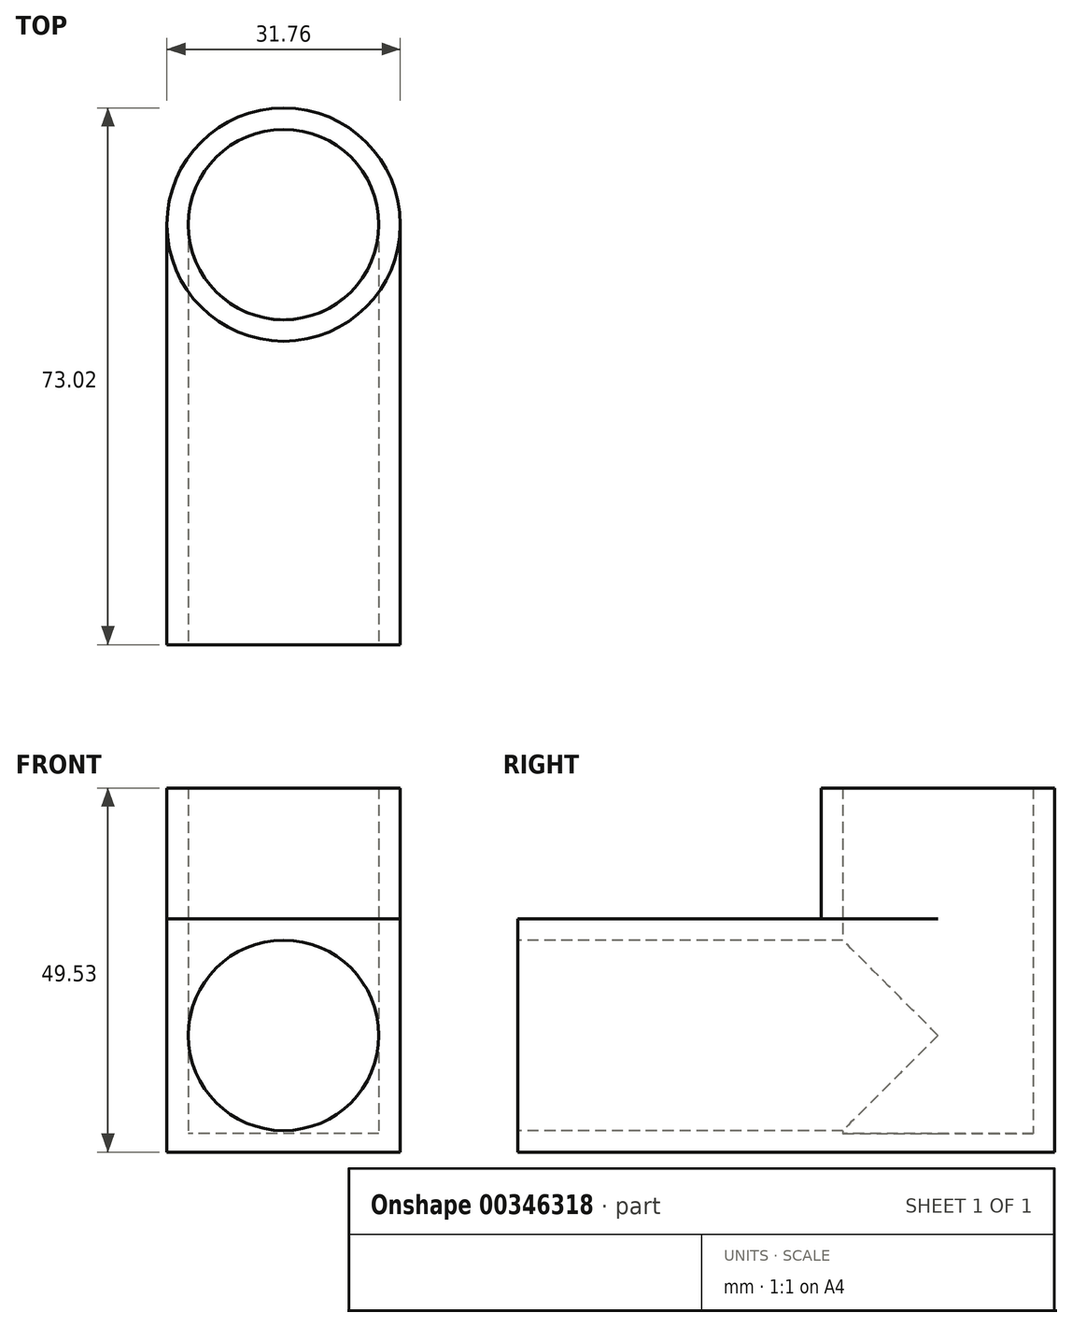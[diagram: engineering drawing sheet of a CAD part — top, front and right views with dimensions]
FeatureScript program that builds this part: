
annotation { "Feature Type Name" : "Feature", "Feature Type Description" : "" }
export const myFeature = defineFeature(function(context is Context, id is Id, definition is map)
    precondition{}
    {
        {
            var Q0;
            Q0=qCreatedBy(makeId("Top.planeOp"),FACE);
            var sketch = newSketch(context, id + "F0", { "sketchPlane" : qUnion([Q0])});
            skLineSegment(sketch, "E0.bottom", {"start": v(15.88, 36.51) * mm, "end": v(-15.87, 36.51) * mm});
            skLineSegment(sketch, "E0.top", {"start": v(15.88, -36.51) * mm, "end": v(-15.88, -36.51) * mm});
            skLineSegment(sketch, "E0.left", {"start": v(15.88, 36.51) * mm, "end": v(15.88, -36.51) * mm});
            skLineSegment(sketch, "E0.right", {"start": v(-15.87, 36.51) * mm, "end": v(-15.88, -36.51) * mm});
            skPoint(sketch, "E0.middle", {"position": v(0, 0) * mm});
            skSolve(sketch);
        }
        {
            var Q0;
            Q0=makeQuery(id+"F0.imprint","IMPRINT",FACE,{"disambiguationData":[TD([[makeQuery(id+"F0.imprint","IMPRINT",EDGE,{"derivedFrom":sQuery(id+"F0.wireOp",EDGE,"E0.bottom")}),1.0]])]});
            extrude(context, id + "F1", {"entities" : qUnion([Q0]), "depth" : 31.75 * mm});
        }
        {
            var Q0;
            Q0=makeQuery(id+"F1.opExtrude","CAP_FACE",FACE,{"disambiguationData":[OSD([sQuery(id+"F0.wireOp",EDGE,"E0.bottom"),sQuery(id+"F0.wireOp",EDGE,"E0.top"),sQuery(id+"F0.wireOp",EDGE,"E0.left"),sQuery(id+"F0.wireOp",EDGE,"E0.right")])],"isStart":false});
            var sketch = newSketch(context, id + "F2", { "sketchPlane" : qUnion([Q0])});
            skCircle(sketch, "E1", {"center": v(0, 20.64) * mm, "radius": 15.88 * mm});
            skCircle(sketch, "E2", {"center": v(0, 20.64) * mm, "radius": 12.95 * mm});
            skSolve(sketch);
        }
        {
            var Q0;
            Q0 = qSketchRegion(id + "F2", true);
            extrude(context, id + "F3", {"entities" : qUnion([Q0]), "operationType" : NewBodyOperationType.ADD, "depth" : 17.78 * mm});
        }
        {
            var Q0;
            {var subQ0=sQuery(id+"F0.wireOp",EDGE,"E0.bottom");var subQ1=sQuery(id+"F0.wireOp",EDGE,"E0.right");var subQ2=makeQuery(id+"F1.opExtrude","CAP_FACE",FACE,{"disambiguationData":[OSD([subQ0,sQuery(id+"F0.wireOp",EDGE,"E0.top"),sQuery(id+"F0.wireOp",EDGE,"E0.left"),subQ1])],"isStart":false});Q0=makeQuery(id+"F3.boolean.opBoolean","SPLIT",FACE,{"disambiguationData":[TD([makeQuery(id+"F1.opExtrude","SWEPT_FACE",FACE,{"disambiguationData":[OSD([subQ0])]}),subQ2,makeQuery(id+"F1.opExtrude","SWEPT_FACE",FACE,{"disambiguationData":[OSD([subQ1])]}),makeQuery(id+"F3.opExtrude","SWEPT_FACE",FACE,{"disambiguationData":[OSD([sQuery(id+"F2.wireOp",EDGE,"E1")])]})])],"derivedFrom":subQ2});}
            extrude(context, id + "F4", {"entities" : qUnion([Q0]), "operationType" : NewBodyOperationType.REMOVE, "endBound" : BoundingType.THROUGH_ALL, "oppositeDirection" : true, "depth" : 25.4 * mm});
        }
        {
            var Q0;
            {var subQ0=sQuery(id+"F0.wireOp",EDGE,"E0.bottom");var subQ1=sQuery(id+"F0.wireOp",EDGE,"E0.left");var subQ2=makeQuery(id+"F1.opExtrude","CAP_FACE",FACE,{"disambiguationData":[OSD([subQ0,sQuery(id+"F0.wireOp",EDGE,"E0.top"),subQ1,sQuery(id+"F0.wireOp",EDGE,"E0.right")])],"isStart":false});Q0=makeQuery(id+"F3.boolean.opBoolean","SPLIT",FACE,{"disambiguationData":[TD([makeQuery(id+"F1.opExtrude","SWEPT_FACE",FACE,{"disambiguationData":[OSD([subQ0])]}),subQ2,makeQuery(id+"F1.opExtrude","SWEPT_FACE",FACE,{"disambiguationData":[OSD([subQ1])]}),makeQuery(id+"F3.opExtrude","SWEPT_FACE",FACE,{"disambiguationData":[OSD([sQuery(id+"F2.wireOp",EDGE,"E1")])]})])],"derivedFrom":subQ2});}
            extrude(context, id + "F5", {"entities" : qUnion([Q0]), "operationType" : NewBodyOperationType.REMOVE, "endBound" : BoundingType.THROUGH_ALL, "oppositeDirection" : true, "depth" : 25.4 * mm});
        }
        {
            var Q0;
            Q0=makeQuery(id+"F3.boolean.opBoolean","SPLIT",FACE,{"disambiguationData":[TD([makeQuery(id+"F3.opExtrude","SWEPT_FACE",FACE,{"disambiguationData":[OSD([sQuery(id+"F2.wireOp",EDGE,"E2")])]})])],"derivedFrom":makeQuery(id+"F1.opExtrude","CAP_FACE",FACE,{"disambiguationData":[OSD([sQuery(id+"F0.wireOp",EDGE,"E0.bottom"),sQuery(id+"F0.wireOp",EDGE,"E0.top"),sQuery(id+"F0.wireOp",EDGE,"E0.left"),sQuery(id+"F0.wireOp",EDGE,"E0.right")])],"isStart":false})});
            extrude(context, id + "F6", {"entities" : qUnion([Q0]), "operationType" : NewBodyOperationType.REMOVE, "oppositeDirection" : true, "depth" : 29.2 * mm});
        }
        {
            var Q0;
            Q0=makeQuery(id+"F1.opExtrude","SWEPT_FACE",FACE,{"disambiguationData":[OSD([sQuery(id+"F0.wireOp",EDGE,"E0.top")])]});
            var sketch = newSketch(context, id + "F7", { "sketchPlane" : qUnion([Q0])});
            skCircle(sketch, "E3", {"center": v(0, 15.88) * mm, "radius": 12.95 * mm});
            skPoint(sketch, "E3.centerSnap0", {"position": v(-15.88, 15.88) * mm});
            skSolve(sketch);
        }
        {
            var Q0;
            Q0 = qSketchRegion(id + "F7", true);
            extrude(context, id + "F8", {"entities" : qUnion([Q0]), "operationType" : NewBodyOperationType.REMOVE, "oppositeDirection" : true, "depth" : 57.15 * mm});
        }
    });
